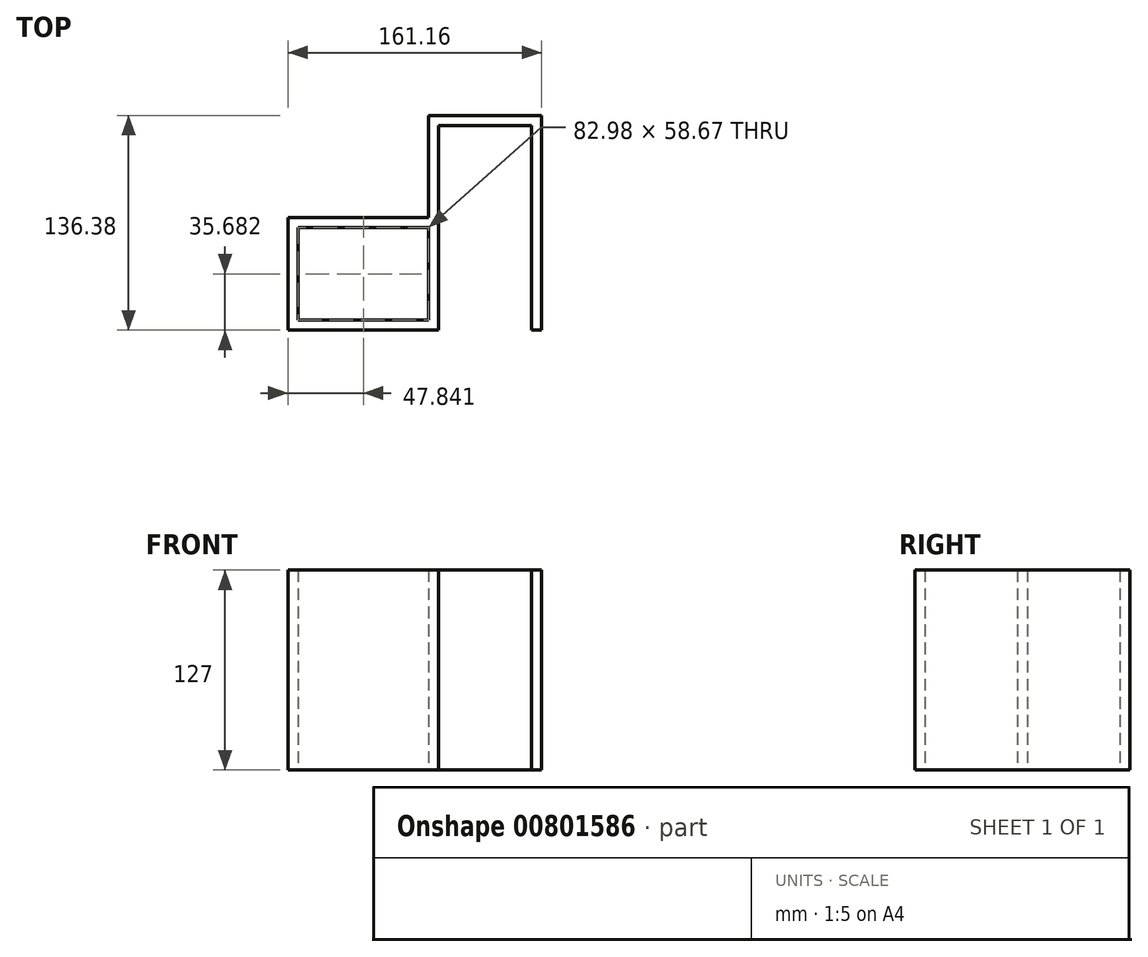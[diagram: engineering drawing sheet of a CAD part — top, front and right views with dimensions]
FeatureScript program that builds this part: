
annotation { "Feature Type Name" : "Feature", "Feature Type Description" : "" }
export const myFeature = defineFeature(function(context is Context, id is Id, definition is map)
    precondition{}
    {
        {
            var Q0;
            Q0=qCreatedBy(makeId("Top.planeOp"),FACE);
            var sketch = newSketch(context, id + "F0", { "sketchPlane" : qUnion([Q0])});
            skLineSegment(sketch, "E0.bottom", {"start": v(-117.63, 12.39) * mm, "end": v(-28.3, 12.39) * mm});
            skLineSegment(sketch, "E0.top", {"start": v(-117.63, -58.98) * mm, "end": v(-28.3, -58.98) * mm});
            skLineSegment(sketch, "E0.left", {"start": v(-117.63, 12.39) * mm, "end": v(-117.63, -58.98) * mm});
            skLineSegment(sketch, "E0.right", {"start": v(-28.3, 12.39) * mm, "end": v(-28.3, -58.98) * mm});
            skLineSegment(sketch, "E1.bottom", {"start": v(-28.3, -58.98) * mm, "end": v(43.53, -58.98) * mm});
            skLineSegment(sketch, "E1.top", {"start": v(-28.3, 77.4) * mm, "end": v(43.53, 77.4) * mm});
            skLineSegment(sketch, "E1.left", {"start": v(-28.3, -58.98) * mm, "end": v(-28.3, 77.4) * mm});
            skLineSegment(sketch, "E1.right", {"start": v(43.53, -58.98) * mm, "end": v(43.53, 77.4) * mm});
            skLineSegment(sketch, "E2.0", {"start": v(37.18, -58.98) * mm, "end": v(37.18, 71.05) * mm});
            skLineSegment(sketch, "E2.1", {"start": v(-21.95, 71.05) * mm, "end": v(37.18, 71.05) * mm});
            skLineSegment(sketch, "E2.2", {"start": v(-21.95, -58.98) * mm, "end": v(-21.95, 71.05) * mm});
            skLineSegment(sketch, "E3.0", {"start": v(-111.28, 6.04) * mm, "end": v(-28.3, 6.04) * mm});
            skLineSegment(sketch, "E3.1", {"start": v(-111.28, 6.04) * mm, "end": v(-111.28, -52.63) * mm});
            skLineSegment(sketch, "E3.2", {"start": v(-111.28, -52.63) * mm, "end": v(-28.3, -52.63) * mm});
            skSolve(sketch);
        }
        {
            var Q0;
            {var subQ4=sQuery(id+"F0.wireOp",EDGE,"E1.top");Q0=makeQuery(id+"F0.imprint","IMPRINT",FACE,{"disambiguationData":[TD([[makeQuery(id+"F0.imprint","IMPRINT",EDGE,{"derivedFrom":subQ4}),-1.0]])]});}
            var Q1;
            {var subQ3=sQuery(id+"F0.wireOp",EDGE,"E0.bottom");Q1=makeQuery(id+"F0.imprint","IMPRINT",FACE,{"disambiguationData":[TD([[makeQuery(id+"F0.imprint","IMPRINT",EDGE,{"derivedFrom":subQ3}),-1.0]])]});}
            extrude(context, id + "F1", {"entities" : qUnion([Q0, Q1]), "depth" : 127 * mm, "offsetDistance" : 25.4 * mm});
        }
    });
